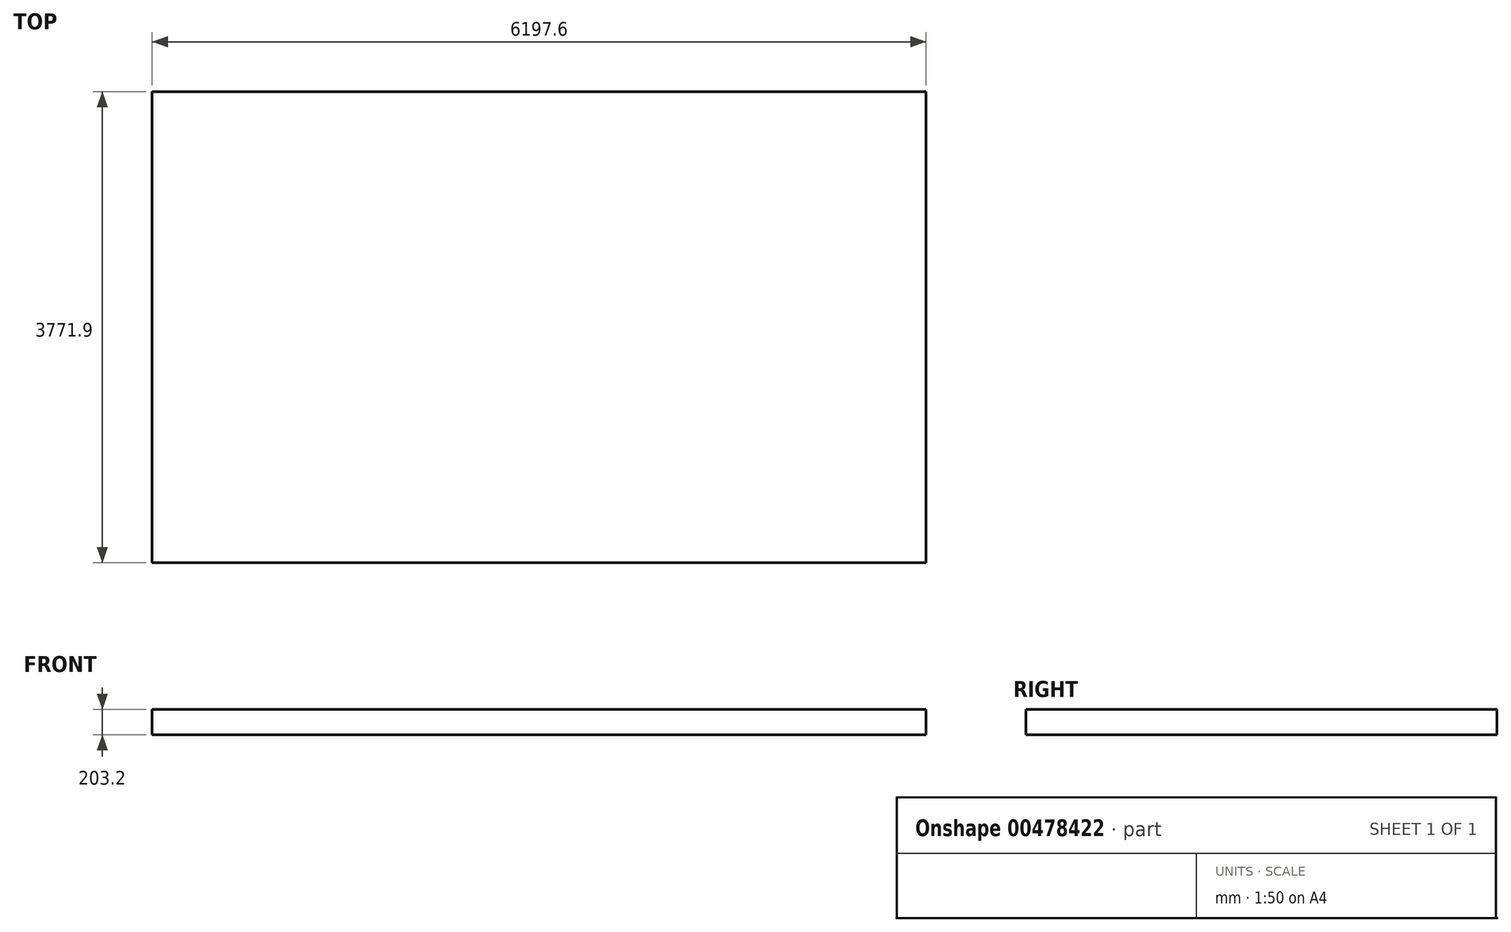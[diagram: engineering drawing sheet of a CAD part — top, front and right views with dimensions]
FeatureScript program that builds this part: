
annotation { "Feature Type Name" : "Feature", "Feature Type Description" : "" }
export const myFeature = defineFeature(function(context is Context, id is Id, definition is map)
    precondition{}
    {
        {
            var Q0;
            Q0=qCreatedBy(makeId("Top.planeOp"),FACE);
            var sketch = newSketch(context, id + "F0", { "sketchPlane" : qUnion([Q0])});
            skLineSegment(sketch, "E0.bottom", {"start": v(3098.8, -1885.95) * mm, "end": v(-3098.8, -1885.95) * mm});
            skLineSegment(sketch, "E0.top", {"start": v(3098.8, 1885.95) * mm, "end": v(-3098.8, 1885.95) * mm});
            skLineSegment(sketch, "E0.left", {"start": v(3098.8, -1885.95) * mm, "end": v(3098.8, 1885.95) * mm});
            skLineSegment(sketch, "E0.right", {"start": v(-3098.8, -1885.95) * mm, "end": v(-3098.8, 1885.95) * mm});
            skPoint(sketch, "E0.middle", {"position": v(0, 0) * mm});
            skSolve(sketch);
        }
        {
            var Q0;
            Q0 = qSketchRegion(id + "F0", true);
            extrude(context, id + "F1", {"entities" : qUnion([Q0]), "depth" : 203.2 * mm});
        }
    });
